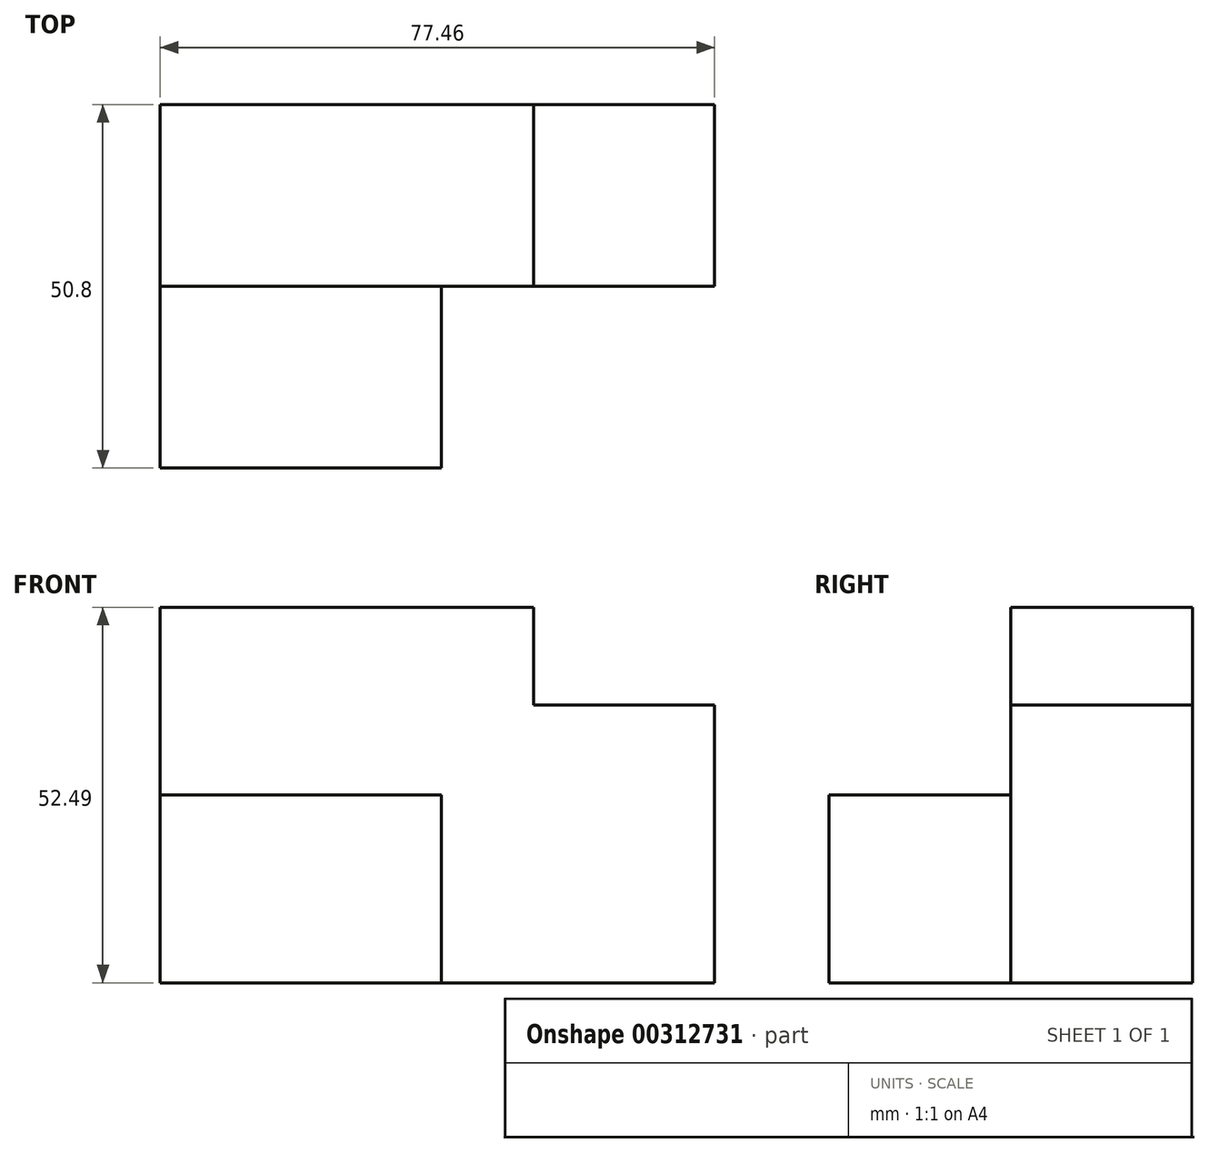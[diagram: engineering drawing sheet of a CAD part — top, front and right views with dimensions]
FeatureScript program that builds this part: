
annotation { "Feature Type Name" : "Feature", "Feature Type Description" : "" }
export const myFeature = defineFeature(function(context is Context, id is Id, definition is map)
    precondition{}
    {
        {
            var Q0;
            Q0=qCreatedBy(makeId("Front.planeOp"),FACE);
            var sketch = newSketch(context, id + "F0", { "sketchPlane" : qUnion([Q0])});
            skLineSegment(sketch, "E0", {"start": v(-57.17, -35.18) * mm, "end": v(20.29, -35.18) * mm});
            skLineSegment(sketch, "E1", {"start": v(-57.17, -35.18) * mm, "end": v(-57.17, 17.3) * mm});
            skLineSegment(sketch, "E2", {"start": v(20.29, -35.18) * mm, "end": v(20.29, 3.69) * mm});
            skLineSegment(sketch, "E3", {"start": v(-57.17, 17.3) * mm, "end": v(-4.97, 17.3) * mm});
            skLineSegment(sketch, "E4", {"start": v(-4.97, 17.3) * mm, "end": v(-4.97, 3.69) * mm});
            skLineSegment(sketch, "E5", {"start": v(-4.97, 3.69) * mm, "end": v(20.29, 3.69) * mm});
            skSolve(sketch);
        }
        {
            var Q0;
            Q0=makeQuery(id+"F0.imprint","IMPRINT",FACE,{"disambiguationData":[TD([[makeQuery(id+"F0.imprint","IMPRINT",EDGE,{"derivedFrom":sQuery(id+"F0.wireOp",EDGE,"E0")}),1.0]])]});
            extrude(context, id + "F1", {"entities" : qUnion([Q0]), "depth" : 25.4 * mm});
        }
        {
            var Q0;
            Q0=makeQuery(id+"F1.opExtrude","CAP_FACE",FACE,{"disambiguationData":[OSD([sQuery(id+"F0.wireOp",EDGE,"E0"),sQuery(id+"F0.wireOp",EDGE,"E1"),sQuery(id+"F0.wireOp",EDGE,"E2"),sQuery(id+"F0.wireOp",EDGE,"E3"),sQuery(id+"F0.wireOp",EDGE,"E4"),sQuery(id+"F0.wireOp",EDGE,"E5")])],"isStart":false});
            var sketch = newSketch(context, id + "F2", { "sketchPlane" : qUnion([Q0])});
            skLineSegment(sketch, "E6", {"start": v(-57.17, -35.18) * mm, "end": v(-57.17, -8.94) * mm});
            skLineSegment(sketch, "E7", {"start": v(-57.17, -8.94) * mm, "end": v(-17.87, -8.94) * mm});
            skLineSegment(sketch, "E8", {"start": v(-17.87, -8.94) * mm, "end": v(-17.87, -35.18) * mm});
            skPoint(sketch, "E8.endSnap0", {"position": v(-18.44, -35.18) * mm});
            skLineSegment(sketch, "E9", {"start": v(-17.87, -35.18) * mm, "end": v(-57.17, -35.18) * mm});
            skSolve(sketch);
        }
        {
            var Q0;
            Q0=makeQuery(id+"F2.imprint","IMPRINT",FACE,{"disambiguationData":[TD([[makeQuery(id+"F2.imprint","IMPRINT",EDGE,{"derivedFrom":sQuery(id+"F2.wireOp",EDGE,"E6")}),-1.0]])]});
            extrude(context, id + "F3", {"entities" : qUnion([Q0]), "operationType" : NewBodyOperationType.ADD, "depth" : 25.4 * mm});
        }
    });
